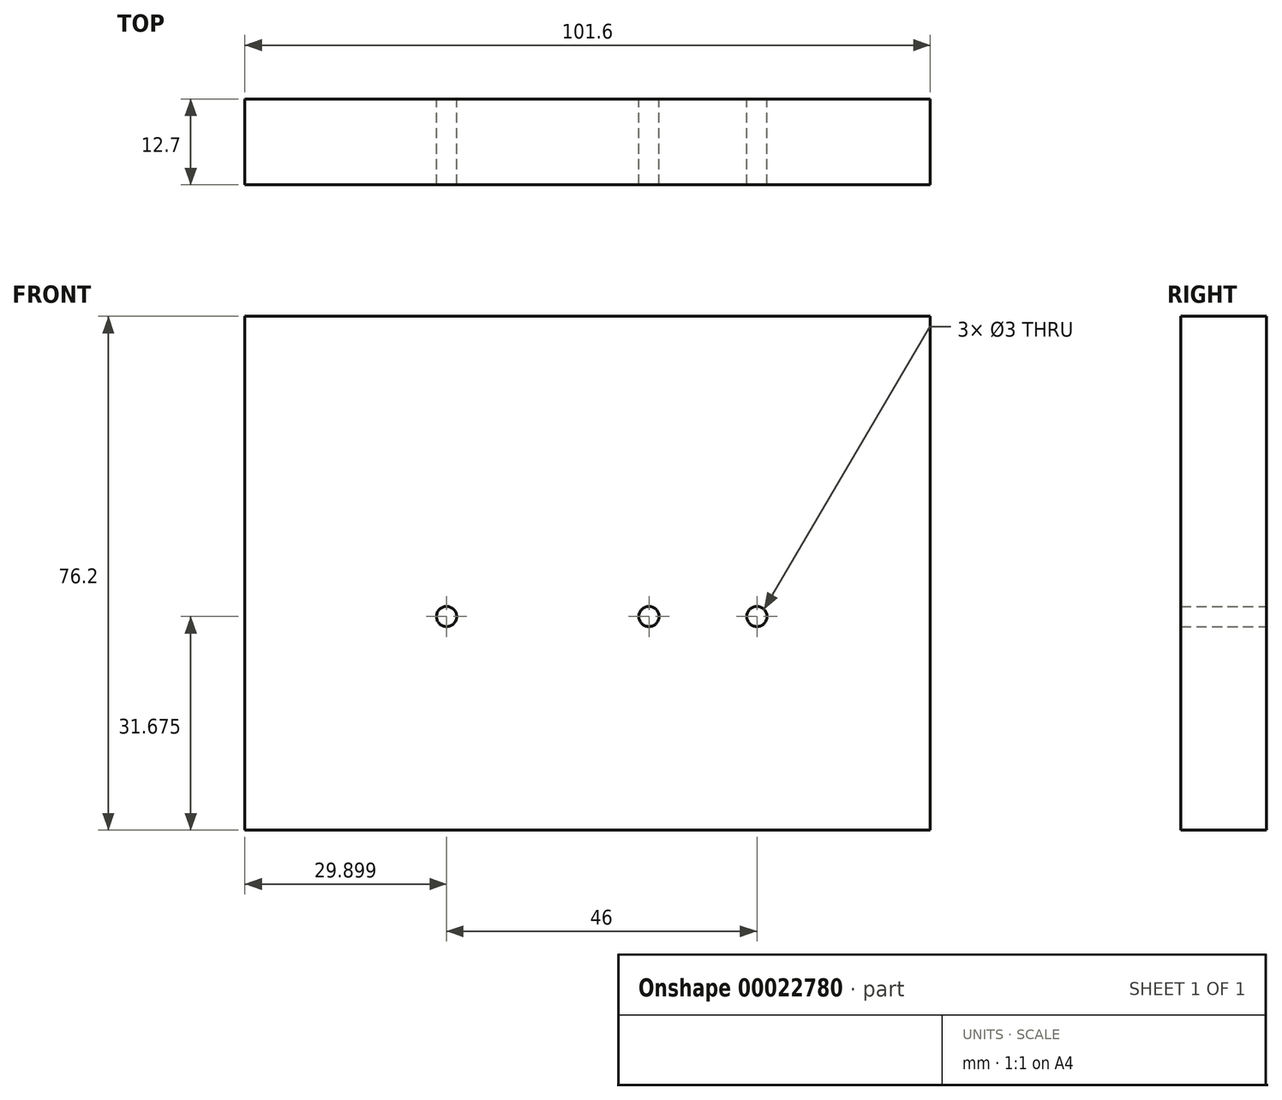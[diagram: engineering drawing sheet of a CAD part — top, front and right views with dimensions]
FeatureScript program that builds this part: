
annotation { "Feature Type Name" : "Feature", "Feature Type Description" : "" }
export const myFeature = defineFeature(function(context is Context, id is Id, definition is map)
    precondition{}
    {
        {
            var Q0;
            Q0=qCreatedBy(makeId("Front.planeOp"),FACE);
            var sketch = newSketch(context, id + "F0", { "sketchPlane" : qUnion([Q0])});
            skLineSegment(sketch, "E0.bottom", {"start": v(-54.41, 41.67) * mm, "end": v(47.19, 41.67) * mm});
            skLineSegment(sketch, "E0.top", {"start": v(-54.41, -34.53) * mm, "end": v(47.19, -34.53) * mm});
            skLineSegment(sketch, "E0.left", {"start": v(-54.41, 41.67) * mm, "end": v(-54.41, -34.53) * mm});
            skLineSegment(sketch, "E0.right", {"start": v(47.19, 41.67) * mm, "end": v(47.19, -34.53) * mm});
            skLineSegment(sketch, "E1", {"start": v(-24.51, -2.85) * mm, "end": v(21.49, -2.85) * mm});
            skLineSegment(sketch, "E2", {"start": v(5.49, -2.85) * mm, "end": v(21.49, -2.85) * mm});
            skCircle(sketch, "E3", {"center": v(-24.51, -2.85) * mm, "radius": 1.5 * mm});
            skCircle(sketch, "E4", {"center": v(5.49, -2.85) * mm, "radius": 1.5 * mm});
            skCircle(sketch, "E5", {"center": v(21.49, -2.85) * mm, "radius": 1.5 * mm});
            skSolve(sketch);
        }
        {
            var Q0;
            Q0 = qSketchRegion(id + "F0", true);
            extrude(context, id + "F1", {"entities" : qUnion([Q0]), "depth" : 12.7 * mm});
        }
    });
